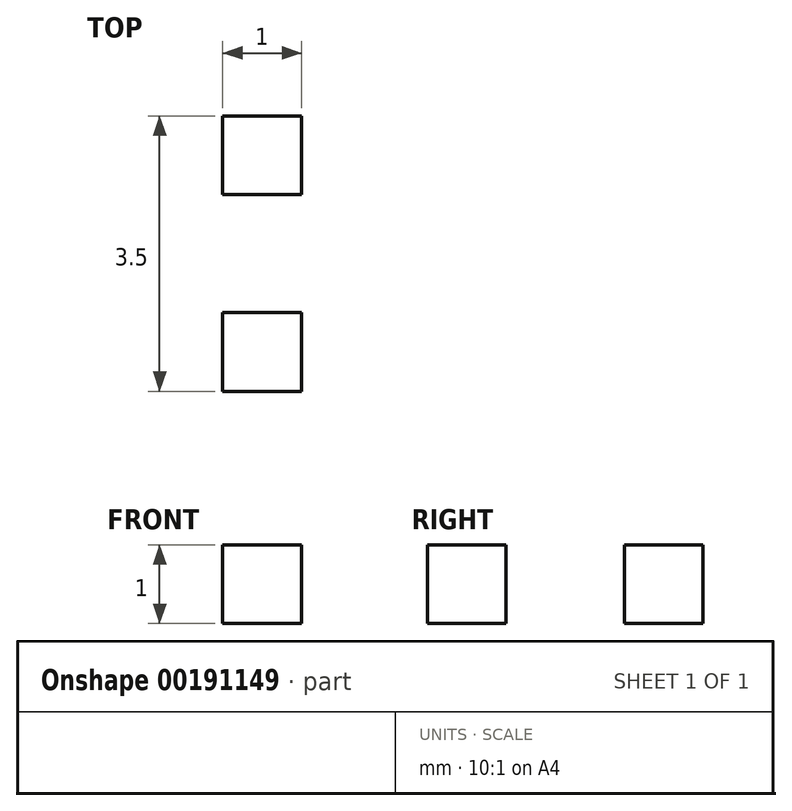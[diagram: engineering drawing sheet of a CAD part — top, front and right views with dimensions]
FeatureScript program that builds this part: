
annotation { "Feature Type Name" : "Feature", "Feature Type Description" : "" }
export const myFeature = defineFeature(function(context is Context, id is Id, definition is map)
    precondition{}
    {
        {
            var Q0;
            Q0=qCreatedBy(makeId("Front.planeOp"),FACE);
            var sketch = newSketch(context, id + "F0", { "sketchPlane" : qUnion([Q0])});
            skLineSegment(sketch, "E0.bottom", {"start": v(0.5, 0.5) * mm, "end": v(-0.5, 0.5) * mm});
            skLineSegment(sketch, "E0.top", {"start": v(0.5, -0.5) * mm, "end": v(-0.5, -0.5) * mm});
            skLineSegment(sketch, "E0.left", {"start": v(0.5, 0.5) * mm, "end": v(0.5, -0.5) * mm});
            skLineSegment(sketch, "E0.right", {"start": v(-0.5, 0.5) * mm, "end": v(-0.5, -0.5) * mm});
            skPoint(sketch, "E0.middle", {"position": v(0, 0) * mm});
            skSolve(sketch);
        }
        {
            var Q0;
            Q0 = qSketchRegion(id + "F0", true);
            extrude(context, id + "F1", {"entities" : qUnion([Q0]), "depth" : 1 * mm});
        }
        {
            var Q0;
            Q0=qCreatedBy(makeId("Right.planeOp"),FACE);
            var sketch = newSketch(context, id + "F2", { "sketchPlane" : qUnion([Q0])});
            skLineSegment(sketch, "E1.bottom", {"start": v(2.5, 0.5) * mm, "end": v(1.5, 0.5) * mm});
            skLineSegment(sketch, "E1.top", {"start": v(2.5, -0.5) * mm, "end": v(1.5, -0.5) * mm});
            skLineSegment(sketch, "E1.left", {"start": v(2.5, 0.5) * mm, "end": v(2.5, -0.5) * mm});
            skLineSegment(sketch, "E1.right", {"start": v(1.5, 0.5) * mm, "end": v(1.5, -0.5) * mm});
            skPoint(sketch, "E1.middle", {"position": v(2, 0) * mm});
            skSolve(sketch);
        }
        {
            var Q0;
            Q0 = qSketchRegion(id + "F2", true);
            extrude(context, id + "F3", {"entities" : qUnion([Q0]), "depth" : 0.5 * mm, "hasSecondDirection" : true, "secondDirectionOppositeDirection" : true, "secondDirectionDepth" : 0.5 * mm});
        }
    });
